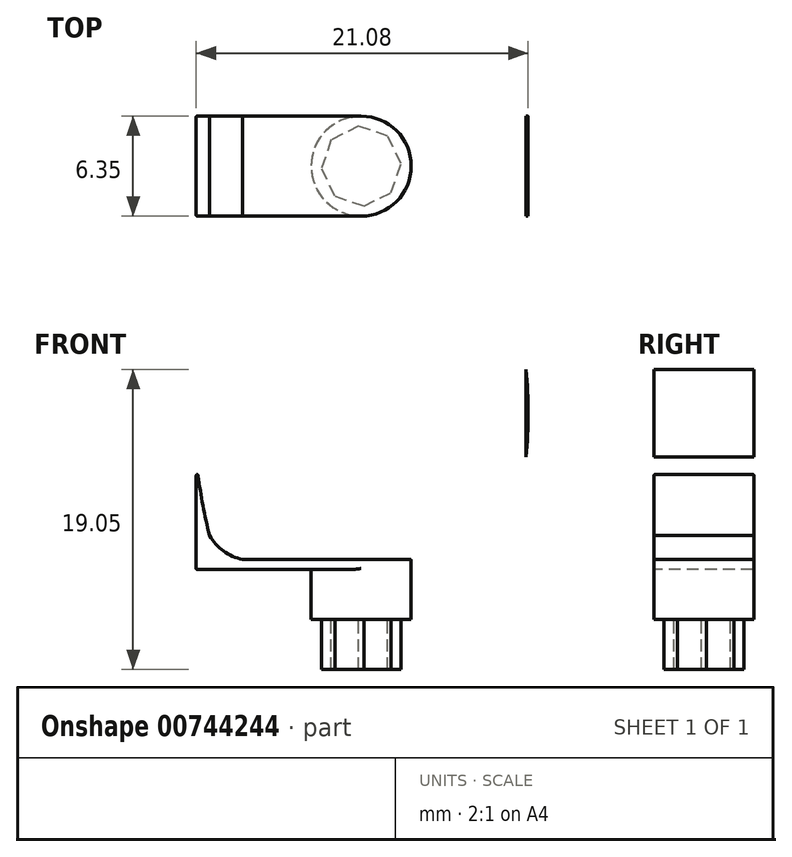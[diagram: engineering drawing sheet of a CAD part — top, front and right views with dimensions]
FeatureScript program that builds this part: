
annotation { "Feature Type Name" : "Feature", "Feature Type Description" : "" }
export const myFeature = defineFeature(function(context is Context, id is Id, definition is map)
    precondition{}
    {
        {
            var Q0;
            Q0=qCreatedBy(makeId("Top.planeOp"),FACE);
            var sketch = newSketch(context, id + "F0", { "sketchPlane" : qUnion([Q0])});
            skLineSegment(sketch, "E0.bottom", {"start": v(-120.36, -11.52) * mm, "end": v(-141.32, -11.52) * mm});
            skLineSegment(sketch, "E0.top", {"start": v(-120.36, -5.17) * mm, "end": v(-141.32, -5.17) * mm});
            skLineSegment(sketch, "E0.left", {"start": v(-120.36, -11.52) * mm, "end": v(-120.36, -5.17) * mm});
            skLineSegment(sketch, "E0.right", {"start": v(-141.32, -11.52) * mm, "end": v(-141.32, -5.17) * mm});
            skLineSegment(sketch, "E1", {"start": v(-140.05, -11.52) * mm, "end": v(-140.05, -5.17) * mm});
            skLineSegment(sketch, "E2", {"start": v(-121.63, -11.52) * mm, "end": v(-121.63, -5.17) * mm});
            skLineSegment(sketch, "E3", {"start": v(-141.32, -8.35) * mm, "end": v(-120.36, -8.35) * mm, "construction": true});
            skLineSegment(sketch, "E4", {"start": v(-130.84, -5.17) * mm, "end": v(-130.84, -11.52) * mm, "construction": true});
            skCircle(sketch, "E5", {"center": v(-130.84, -8.35) * mm, "radius": 3.17 * mm});
            skLineSegment(sketch, "E6", {"start": v(-121.63, -8.35) * mm, "end": v(-127.66, -8.35) * mm});
            skLineSegment(sketch, "E7", {"start": v(-127.66, -8.35) * mm, "end": v(-121.63, -8.35) * mm});
            skLineSegment(sketch, "E8", {"start": v(-140.05, -8.35) * mm, "end": v(-134.01, -8.35) * mm});
            skSolve(sketch);
        }
        {
            var Q0;
            {var subQ0=sQuery(id+"F0.wireOp",EDGE,"E5");var subQ1=makeQuery(id+"F0.imprint","INTERSECT",VERTEX,{"derivedFrom":[subQ0,sQuery(id+"F0.wireOp",EDGE,"E7")]});Q0=makeQuery(id+"F0.imprint","IMPRINT",FACE,{"disambiguationData":[TD([[makeQuery(id+"F0.imprint","IMPRINT",EDGE,{"disambiguationData":[TD([[subQ1,-1.0]])],"derivedFrom":subQ0}),1.0]])]});}
            extrude(context, id + "F1", {"entities" : qUnion([Q0]), "oppositeDirection" : true, "depth" : 3.17 * mm, "offsetDistance" : 25.4 * mm});
        }
        {
            var Q0;
            {var subQ5=sQuery(id+"F0.wireOp",EDGE,"E8");Q0=makeQuery(id+"F0.imprint","IMPRINT",FACE,{"disambiguationData":[TD([[makeQuery(id+"F0.imprint","IMPRINT",EDGE,{"derivedFrom":subQ5}),1.0]])]});}
            var Q1;
            {var subQ5=sQuery(id+"F0.wireOp",EDGE,"E7");Q1=makeQuery(id+"F0.imprint","IMPRINT",FACE,{"disambiguationData":[TD([[makeQuery(id+"F0.imprint","IMPRINT",EDGE,{"derivedFrom":subQ5}),1.0]])]});}
            var Q2;
            {var subQ5=sQuery(id+"F0.wireOp",EDGE,"E7");Q2=makeQuery(id+"F0.imprint","IMPRINT",FACE,{"disambiguationData":[TD([[makeQuery(id+"F0.imprint","IMPRINT",EDGE,{"derivedFrom":subQ5}),-1.0]])]});}
            var Q3;
            {var subQ5=sQuery(id+"F0.wireOp",EDGE,"E8");Q3=makeQuery(id+"F0.imprint","IMPRINT",FACE,{"disambiguationData":[TD([[makeQuery(id+"F0.imprint","IMPRINT",EDGE,{"derivedFrom":subQ5}),-1.0]])]});}
            var Q4;
            {var subQ0=sQuery(id+"F0.wireOp",EDGE,"E5");var subQ1=makeQuery(id+"F0.imprint","INTERSECT",VERTEX,{"derivedFrom":[subQ0,sQuery(id+"F0.wireOp",EDGE,"E7")]});Q4=makeQuery(id+"F0.imprint","IMPRINT",FACE,{"disambiguationData":[TD([[makeQuery(id+"F0.imprint","IMPRINT",EDGE,{"disambiguationData":[TD([[subQ1,-1.0]])],"derivedFrom":subQ0}),1.0]])]});}
            extrude(context, id + "F2", {"entities" : qUnion([Q0, Q1, Q2, Q3, Q4]), "operationType" : NewBodyOperationType.ADD, "depth" : 0.64 * mm, "offsetDistance" : 25.4 * mm});
        }
        {
            var Q0;
            {var subQ0=sQuery(id+"F0.wireOp",EDGE,"E0.bottom");Q0=makeQuery(id+"FpU9zEvWotgcPLu_1.boolean.opBoolean","MERGE",FACE,{"derivedFrom":[makeQuery(id+"F2.opExtrude","SWEPT_FACE",FACE,{"disambiguationData":[OSD([subQ0])]}),makeQuery(id+"FpU9zEvWotgcPLu_1.opExtrude","SWEPT_FACE",FACE,{"disambiguationData":[OSD([subQ0]),TDD([makeQuery(id+"F0.imprint","IMPRINT",EDGE,{"disambiguationData":[TD([[makeQuery(id+"F0.imprint","INTERSECT",VERTEX,{"derivedFrom":[subQ0,sQuery(id+"F0.wireOp",EDGE,"E0.left")]}),-1.0]])],"derivedFrom":subQ0})])]}),makeQuery(id+"FpU9zEvWotgcPLu_1.opExtrude","SWEPT_FACE",FACE,{"disambiguationData":[OSD([subQ0]),TDD([makeQuery(id+"F0.imprint","IMPRINT",EDGE,{"disambiguationData":[TD([[makeQuery(id+"F0.imprint","INTERSECT",VERTEX,{"derivedFrom":[subQ0,sQuery(id+"F0.wireOp",EDGE,"E0.right")]}),1.0]])],"derivedFrom":subQ0})])]})]});}
            var sketch = newSketch(context, id + "F3", { "sketchPlane" : qUnion([Q0])});
            skArc(sketch, "E9", {"start": v(-141.32, 12.7) * mm, "mid": v(-141.26, 6.6) * mm, "end": v(-140.05, 0.64) * mm});
            skLineSegment(sketch, "E10", {"start": v(-130.84, 0.64) * mm, "end": v(-130.84, 0) * mm, "construction": true});
            skArc(sketch, "E11.MirrorCS", {"start": v(-120.36, 12.7) * mm, "mid": v(-120.42, 6.6) * mm, "end": v(-121.63, 0.64) * mm});
            skLineSegment(sketch, "E12", {"start": v(-120.36, 12.7) * mm, "end": v(-120.36, 0) * mm});
            skLineSegment(sketch, "E13", {"start": v(-141.32, 12.7) * mm, "end": v(-141.32, 0) * mm});
            skLineSegment(sketch, "E14.bottom", {"start": v(-140.05, 0.64) * mm, "end": v(-141.32, 0.64) * mm});
            skLineSegment(sketch, "E14.top", {"start": v(-140.05, 0) * mm, "end": v(-141.32, 0) * mm});
            skLineSegment(sketch, "E14.left", {"start": v(-140.05, 0.64) * mm, "end": v(-140.05, 0) * mm});
            skLineSegment(sketch, "E14.right", {"start": v(-141.32, 0.64) * mm, "end": v(-141.32, 0) * mm});
            skLineSegment(sketch, "E15.MirrorCS", {"start": v(-120.36, 0.64) * mm, "end": v(-120.36, 0) * mm});
            skLineSegment(sketch, "E16.MirrorCS", {"start": v(-121.63, 0.64) * mm, "end": v(-120.36, 0.64) * mm});
            skLineSegment(sketch, "E17.MirrorCS", {"start": v(-121.63, 0) * mm, "end": v(-120.36, 0) * mm});
            skLineSegment(sketch, "E18.MirrorCS", {"start": v(-121.63, 0.64) * mm, "end": v(-121.63, 0) * mm});
            skArc(sketch, "E19", {"start": v(-140.47, 2.15) * mm, "mid": v(-139.59, 1.17) * mm, "end": v(-138.37, 0.64) * mm});
            skArc(sketch, "E20.MirrorCS", {"start": v(-121.2, 2.15) * mm, "mid": v(-122.1, 1.17) * mm, "end": v(-123.3, 0.64) * mm});
            skSolve(sketch);
        }
        {
            var Q0;
            Q0=makeQuery(id+"F3.imprint","IMPRINT",FACE,{"disambiguationData":[TD([[makeQuery(id+"F3.imprint","IMPRINT",EDGE,{"derivedFrom":sQuery(id+"F3.wireOp",EDGE,"E9")}),-1.0]])]});
            var Q1;
            Q1=makeQuery(id+"F3.imprint","IMPRINT",FACE,{"disambiguationData":[TD([[makeQuery(id+"F3.imprint","IMPRINT",EDGE,{"derivedFrom":sQuery(id+"F3.wireOp",EDGE,"E14.bottom")}),1.0]])]});
            var Q2;
            Q2=makeQuery(id+"F3.imprint","IMPRINT",FACE,{"disambiguationData":[TD([[makeQuery(id+"F3.imprint","IMPRINT",EDGE,{"derivedFrom":sQuery(id+"F3.wireOp",EDGE,"E15.MirrorCS")}),-1.0]])]});
            var Q3;
            Q3=makeQuery(id+"F3.imprint","IMPRINT",FACE,{"disambiguationData":[TD([[makeQuery(id+"F3.imprint","IMPRINT",EDGE,{"derivedFrom":sQuery(id+"F3.wireOp",EDGE,"E11.MirrorCS")}),1.0]])]});
            var Q4;
            {var subQ3=sQuery(id+"F3.wireOp",EDGE,"DcFVQG6f-j8iD-A8Ef-dXHZ-nHQPqFIMeg8a");Q4=makeQuery(id+"F3.imprint","IMPRINT",FACE,{"disambiguationData":[TD([[makeQuery(id+"F3.imprint","IMPRINT",EDGE,{"derivedFrom":subQ3}),-1.0]])]});}
            var Q5;
            {var subQ3=sQuery(id+"F3.wireOp",EDGE,"E19");Q5=makeQuery(id+"F3.imprint","IMPRINT",FACE,{"disambiguationData":[TD([[makeQuery(id+"F3.imprint","IMPRINT",EDGE,{"derivedFrom":subQ3}),-1.0]])]});}
            var Q6;
            {var subQ3=sQuery(id+"F3.wireOp",EDGE,"E20.MirrorCS");Q6=makeQuery(id+"F3.imprint","IMPRINT",FACE,{"disambiguationData":[TD([[makeQuery(id+"F3.imprint","IMPRINT",EDGE,{"derivedFrom":subQ3}),1.0]])]});}
            extrude(context, id + "F4", {"entities" : qUnion([Q0, Q1, Q2, Q3, Q4, Q5, Q6]), "operationType" : NewBodyOperationType.ADD, "depth" : -6.35 * mm, "offsetDistance" : 25.4 * mm});
        }
        {
            var Q0;
            Q0=makeQuery(id+"F4.opExtrude","SWEPT_EDGE",EDGE,{"disambiguationData":[OSD([sQuery(id+"F3.wireOp",EDGE,"E11.MirrorCS"),sQuery(id+"F3.wireOp",EDGE,"E12")])]});
            var Q1;
            Q1=makeQuery(id+"F4.opExtrude","SWEPT_EDGE",EDGE,{"disambiguationData":[OSD([sQuery(id+"F3.wireOp",EDGE,"E9"),sQuery(id+"F3.wireOp",EDGE,"E13")])]});
            var Q2;
            Q2=makeQuery(id+"F4.opExtrude","CAP_EDGE",EDGE,{"disambiguationData":[OSD([sQuery(id+"F3.wireOp",EDGE,"E12"),sQuery(id+"F3.wireOp",EDGE,"E15.MirrorCS")])],"isStart":true});
            var Q3;
            Q3=makeQuery(id+"F4.opExtrude","CAP_EDGE",EDGE,{"disambiguationData":[OSD([sQuery(id+"F3.wireOp",EDGE,"E12"),sQuery(id+"F3.wireOp",EDGE,"E15.MirrorCS")])],"isStart":false});
            var Q4;
            Q4=makeQuery(id+"F4.opExtrude","SWEPT_FACE",FACE,{"disambiguationData":[OSD([sQuery(id+"F3.wireOp",EDGE,"E12"),sQuery(id+"F3.wireOp",EDGE,"E15.MirrorCS")])]});
            var Q5;
            Q5=makeQuery(id+"F2.opExtrude","CAP_EDGE",EDGE,{"disambiguationData":[OSD([sQuery(id+"F0.wireOp",EDGE,"E0.bottom")])],"isStart":false});
            var Q6;
            Q6=makeQuery(id+"F4.opExtrude","CAP_EDGE",EDGE,{"disambiguationData":[OSD([sQuery(id+"F3.wireOp",EDGE,"E9")])],"isStart":true});
            var Q7;
            Q7=makeQuery(id+"F4.opExtrude","CAP_EDGE",EDGE,{"disambiguationData":[OSD([sQuery(id+"F3.wireOp",EDGE,"E13"),sQuery(id+"F3.wireOp",EDGE,"E14.right")])],"isStart":true});
            var Q8;
            {var subQ0=sQuery(id+"F0.wireOp",EDGE,"E1");var subQ1=sQuery(id+"F0.wireOp",EDGE,"E0.bottom");Q8=makeQuery(id+"F4.boolean.opBoolean","MERGE",EDGE,{"derivedFrom":[makeQuery(id+"F2.boolean.opBoolean","SPLIT",EDGE,{"disambiguationData":[TD([makeQuery(id+"F2.opExtrude","SWEPT_FACE",FACE,{"disambiguationData":[OSD([subQ0])]})])],"derivedFrom":makeQuery(id+"F2.opExtrude","CAP_EDGE",EDGE,{"disambiguationData":[OSD([subQ1])],"isStart":true})}),makeQuery(id+"F4.opExtrude","CAP_EDGE",EDGE,{"disambiguationData":[OSD([sQuery(id+"F3.wireOp",EDGE,"E14.top")])],"isStart":true})]});}
            var Q9;
            {var subQ0=sQuery(id+"F0.wireOp",EDGE,"E0.bottom");var subQ1=sQuery(id+"F0.wireOp",EDGE,"E2");Q9=makeQuery(id+"F4.boolean.opBoolean","MERGE",EDGE,{"derivedFrom":[makeQuery(id+"F2.boolean.opBoolean","SPLIT",EDGE,{"disambiguationData":[TD([makeQuery(id+"F2.opExtrude","SWEPT_FACE",FACE,{"disambiguationData":[OSD([subQ1])]})])],"derivedFrom":makeQuery(id+"F2.opExtrude","CAP_EDGE",EDGE,{"disambiguationData":[OSD([subQ0])],"isStart":true})}),makeQuery(id+"F4.opExtrude","CAP_EDGE",EDGE,{"disambiguationData":[OSD([sQuery(id+"F3.wireOp",EDGE,"E17.MirrorCS")])],"isStart":true})]});}
            var Q10;
            Q10=makeQuery(id+"F4.opExtrude","CAP_EDGE",EDGE,{"disambiguationData":[OSD([sQuery(id+"F3.wireOp",EDGE,"E11.MirrorCS")])],"isStart":false});
            var Q11;
            Q11=makeQuery(id+"F2.opExtrude","CAP_EDGE",EDGE,{"disambiguationData":[OSD([sQuery(id+"F0.wireOp",EDGE,"E0.top")])],"isStart":false});
            var Q12;
            Q12=makeQuery(id+"F4.opExtrude","CAP_EDGE",EDGE,{"disambiguationData":[OSD([sQuery(id+"F3.wireOp",EDGE,"E9")])],"isStart":false});
            var Q13;
            Q13=makeQuery(id+"F4.opExtrude","CAP_EDGE",EDGE,{"disambiguationData":[OSD([sQuery(id+"F3.wireOp",EDGE,"E13"),sQuery(id+"F3.wireOp",EDGE,"E14.right")])],"isStart":false});
            var Q14;
            {var subQ0=sQuery(id+"F0.wireOp",EDGE,"E1");var subQ1=sQuery(id+"F0.wireOp",EDGE,"E0.top");Q14=makeQuery(id+"F4.boolean.opBoolean","MERGE",EDGE,{"derivedFrom":[makeQuery(id+"F2.boolean.opBoolean","SPLIT",EDGE,{"disambiguationData":[TD([makeQuery(id+"F2.opExtrude","SWEPT_FACE",FACE,{"disambiguationData":[OSD([subQ0])]})])],"derivedFrom":makeQuery(id+"F2.opExtrude","CAP_EDGE",EDGE,{"disambiguationData":[OSD([subQ1])],"isStart":true})}),makeQuery(id+"F4.opExtrude","CAP_EDGE",EDGE,{"disambiguationData":[OSD([sQuery(id+"F3.wireOp",EDGE,"E14.top")])],"isStart":false})]});}
            var Q15;
            {var subQ0=sQuery(id+"F0.wireOp",EDGE,"E2");var subQ1=sQuery(id+"F0.wireOp",EDGE,"E0.top");Q15=makeQuery(id+"F4.boolean.opBoolean","MERGE",EDGE,{"derivedFrom":[makeQuery(id+"F2.boolean.opBoolean","SPLIT",EDGE,{"disambiguationData":[TD([makeQuery(id+"F2.opExtrude","SWEPT_FACE",FACE,{"disambiguationData":[OSD([subQ0])]})])],"derivedFrom":makeQuery(id+"F2.opExtrude","CAP_EDGE",EDGE,{"disambiguationData":[OSD([subQ1])],"isStart":true})}),makeQuery(id+"F4.opExtrude","CAP_EDGE",EDGE,{"disambiguationData":[OSD([sQuery(id+"F3.wireOp",EDGE,"E17.MirrorCS")])],"isStart":false})]});}
            var Q16;
            Q16=makeQuery(id+"F4.opExtrude","SWEPT_EDGE",EDGE,{"disambiguationData":[OSD([sQuery(id+"F3.wireOp",EDGE,"E14.top"),sQuery(id+"F3.wireOp",EDGE,"E14.right")])]});
            var Q17;
            Q17=makeQuery(id+"F4.opExtrude","CAP_EDGE",EDGE,{"disambiguationData":[OSD([sQuery(id+"F3.wireOp",EDGE,"E19")])],"isStart":true});
            var Q18;
            Q18=makeQuery(id+"F4.opExtrude","CAP_EDGE",EDGE,{"disambiguationData":[OSD([sQuery(id+"F3.wireOp",EDGE,"E19")])],"isStart":false});
            var Q19;
            Q19=makeQuery(id+"F4.opExtrude","SWEPT_FACE",FACE,{"disambiguationData":[OSD([sQuery(id+"F3.wireOp",EDGE,"E11.MirrorCS")])]});
            fillet(context, id + "F5", {"entities" : qUnion([Q0, Q1, Q2, Q3, Q4, Q5, Q6, Q7, Q8, Q9, Q10, Q11, Q12, Q13, Q14, Q15, Q16, Q17, Q18, Q19]), "radius" : 0.06 * mm, "tangentPropagation" : true, "allowEdgeOverflow" : false});
        }
        {
            var Q0;
            Q0=makeQuery(id+"F1.opExtrude","CAP_FACE",FACE,{"disambiguationData":[OSD([sQuery(id+"F0.wireOp",EDGE,"E5")])],"isStart":false});
            var sketch = newSketch(context, id + "F6", { "sketchPlane" : qUnion([Q0])});
            skCircle(sketch, "E21.cCircle", {"center": v(-130.84, 8.35) * mm, "radius": 2.54 * mm, "construction": true});
            skLineSegment(sketch, "E21.0", {"start": v(-131, 5.81) * mm, "end": v(-132.75, 6.67) * mm});
            skLineSegment(sketch, "E21.1", {"start": v(-132.75, 6.67) * mm, "end": v(-133.37, 8.51) * mm});
            skLineSegment(sketch, "E21.2", {"start": v(-133.37, 8.51) * mm, "end": v(-132.52, 10.26) * mm});
            skLineSegment(sketch, "E21.3", {"start": v(-132.52, 10.26) * mm, "end": v(-130.68, 10.88) * mm});
            skLineSegment(sketch, "E21.4", {"start": v(-130.68, 10.88) * mm, "end": v(-128.93, 10.03) * mm});
            skLineSegment(sketch, "E21.5", {"start": v(-128.93, 10.03) * mm, "end": v(-128.3, 8.19) * mm});
            skLineSegment(sketch, "E21.6", {"start": v(-128.3, 8.19) * mm, "end": v(-129.16, 6.44) * mm});
            skLineSegment(sketch, "E21.7", {"start": v(-129.16, 6.44) * mm, "end": v(-131, 5.81) * mm});
            skSolve(sketch);
        }
        {
            var Q0;
            Q0=makeQuery(id+"F6.imprint","IMPRINT",FACE,{"disambiguationData":[TD([[makeQuery(id+"F6.imprint","IMPRINT",EDGE,{"derivedFrom":sQuery(id+"F6.wireOp",EDGE,"E21.0")}),-1.0]])]});
            extrude(context, id + "F7", {"entities" : qUnion([Q0]), "operationType" : NewBodyOperationType.ADD, "depth" : 3.17 * mm, "offsetDistance" : 25.4 * mm});
        }
    });
